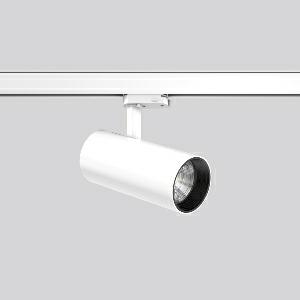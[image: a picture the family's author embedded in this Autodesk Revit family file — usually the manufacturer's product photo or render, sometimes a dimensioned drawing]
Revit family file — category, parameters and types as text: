
# Revit family: deecos_s_mini_742207_002_2_94e4
name_source: partatom
category: Lighting Fixtures
units: mm (PartAtom-declared; Revit-internal decimal feet)

## family parameters
Cut with Voids When Loaded = No
Host = Face
Light Source = No
Part Type = Normal
Room Calculation Point = No
Round Connector Dimension = Use Diameter
Shared = No

## types (1)
- DEECOS S mini (1 x LED Modul 927, 2850 lm, 2700)
    Apparent Load = 29 VA
    Approval mark = CE
    CIE Flux Codes = 96 100 100 100 100
    Color Rendering = 92
    Color Temperature = 2700
    Default Elevation = 1800 mm
    Description = Series: DEECOS S mini
LED surface-mounted projector in modern design with no visible cooling ribs. Housing: die-cast aluminium, powder-coated. Rotation range: 356°. Swivel range: 90°. Black plastic ring and recessed LED to prevent glare from the side. Optical assembly with lens made of plastic (polycarbonate) for the best homogeneous light distribution - can be changed without tools. Best colour rendering index Ra>90. With multi adaptor for 3-circuit tracks 230 V. Suitable for Track on ceiling, Wall track. High quality converter without flickering and stroboscopic effect. The following accessories can be mounted without use of tools: interchangeable lenses, decorative glasses, honeycomb louvre, clear and frosted diffusers, white interchangeable plastic ring. 
Colour: traffic white, matt (RAL 9016)
Diameter: 87 mm
Height: 214 mm
Lamp: LED
Socket: without socket
Colour temperature: 2700K
Colour rendering index (CRI): 92
System power: 29 W
Rated luminous flux: 2850 lm
Luminous efficiency: 98 lm/W
Control gear: Regulated power supply
Protection class: I
Type of protection: IP 20
    Height = 214 mm
    Lamp = 1 x LED Modul 927
    Lamp Light Flux = 2850 lm
    Lamp count = 1
    Length = 87 mm
    Lifetime = 50000 h
    Luminous efficacy = 98 lm/W
    Manufacturer = RZB
    ModVariant = No
    Model = 742207.002.2
    Mounting Place = Ceiling
    Mounting Type = Rail mounted
    Number of Poles = 1
    OnlyDefault = Yes
    Power Factor = 1
    Product Name = DEECOS S mini
    Product group = Track mounted projectors
    ProductGroupID = 301
    Protection Class = Protection class I
    Protection Degree = IP 20
    RLX_Detail_Level = 1
    RLX_Emergency_Light_Flux = 0 lm
    RLX_Emergency_Type = 0
    RLX_Emergency_Type_DB = No
    RlxData = <blob elided: 35357 chars, md5=2e900053>
    Socket = socket
    Standby Power = 0 W
    System Light Flux = 2850 lm
    System Power = 29 W
    Type Comments = Product without accessories
    Type Image = 741930.002.jpg
    URL = http://relux.com
    VarID = ---
    Voltage = 230 V
    Voltage Range = 220-240 V
    Weight = 0.00 kg
    Width = 0 mm  [stored 0 ft]

note: [stored X ft] marks values corroborated as IEEE doubles in the binary element streams (Revit-internal decimal feet)

## geometry (parser evidence)
native form markers: Blend x4, Sweep x14
no freeform markers — native parametric forms only
